# Revit family: Panca WING wood
name_source: partatom
category: Modelli generici
revit_build: Autodesk Revit 2018 (Build: 20170223_1515(x64)
units: mm (PartAtom-declared; Revit-internal decimal feet)

## family parameters
Basato su piano di lavoro = No
Condiviso = No
Punto di calcolo locali = No
Può ospitare armatura = No
Quota connettore circolare = Usa diametro
Sempre verticale = Sì
Taglio con vuoti quando caricato = No
Tipo di parte = Normale

## types (3) — shared parameters
BIM Name = WING WOOD
BIM Object Type = PANCHINE - BENCHES
Code = 0PAAR086
Descrizione Tecnica Famiglia = "La panca mod. ”WING” WOOD, la cui forma rimanda a un ala, è costituita da una seduta monolitica dotata di doghe sagomate a sbalzo che garantisce un confort di seduta alle alte o basse temperature."
Designer = DEL PONTE, ZAMBELLI
Dimensions = 2114 mm X 634 mm X 450 mm
Family Name = WING WOOD
Fissaggio = Barre filettate per ancoraggio a terra
IFC = Furnishing Element
MASTERFORMAT 2014 (DESCRIPTION/CODE) = Benches and seat / 12 67 23
MATERIALE SEDUTA = OKUME
OMNICLASS (DESCRIPTION/CODE) = Exterior Benches / 23-11 29 13 11
Technical Description Family = "The bench mod. ""WING"" WOOD, whose shape refers to a wing, consists of a monolithic seat equipped with cantilevered shaped slats which guarantees a comfort of sitting at high or low temperatures."
UNICLASS 1.4 (DESCRIPTION/CODE) = Benches / L8225
UNICLASS 2.0 (DESCRIPTION/CODE) = Chairs, Seats And Bench Seating / PR-31-12
UNIFORMAT II (DESCRIPTION/CODE) = FURNISHINGS / E20
UNSPSC CATEGORY (CODE) = 56
URL Eng = https://www.bellitalia.net
URL Ita = https://www.bellitalia.net
Weight ( kg) = 382 Kg

## per-type parameters (varying)
| type | Descrizione Tecnica per Codice | Fixings | MATERIALE SUPPORTO | Materiale Principale | Materiale Secondario | Primary Material | Secondary Material | Technical Description for Article |
| 0PAAR086 - GRANITO | PANCA WING WOOD IN GRANITO (COLORE A SCELTA) SABBIATO VERNICIATURA ANTIDEGRADO E SEDUTA IN LEGNO DI OKUME | " Threaded rods for ground anchoring" | GRANITO | Granito Bianco | Granito; Legno Okume | Reconstituted White Granite | Reconstituted Granite; Okume Wood | WING WOOD BENCH IN GRANITO (COLOR TO BE CHOSEN) SANDBLASTED ANTI-DECAY VARNISH AND OKUME WOOD SEAT |
| 0PAAR086 - PIETRE PREZIOSE | PANCA WING WOOD IN PIETRE PREZIOSE (COLORE A SCELTA ECCETTO VERDE ALPI) SABBIATO VERNICIATURA ANTI-DEGRADO E SEDUTA IN LEGNO DI OKUME | "threaded rods for ground anchoring" | PIETRE PREZIOSE | Pietre Preziose Ricostituite Bianco Carrara | Pietre Preziose Ricostituite; Legno Okume | Reconstituted Precious Stones Bianco Carrara | Reconstituted Precious Stones; Okume Wood | WING WOOD BENCH IN PRECIOUS STONES (COLOR TO BE CHOSEN EXCEPT GREEN ALPS) SANDBLASTED ANTI-DECAY VARNISH AND OKUME WOOD SEAT |
| 0PAAR086 - VERDE ALPI | PANCA WING WOOD IN VERDE ALPI SABBIATO VERNICIATURA ANTI-DEGRADO E SEDUTA IN LEGNO DI OKUME | "threaded rods for ground anchoring" | VERDE ALPI | Pietre Preziose Ricostituite Verde Alpi | Pietre Preziose Ricostituite; Legno Okume | Reconstituted Precious Stones Verde Alpi | Reconstituted Precious Stones; Okume Wood | WING WOOD BENCH IN GREEN ALPS SANDBLASTED ANTI-DECAY VARNISH AND OKUME WOOD SEAT |
